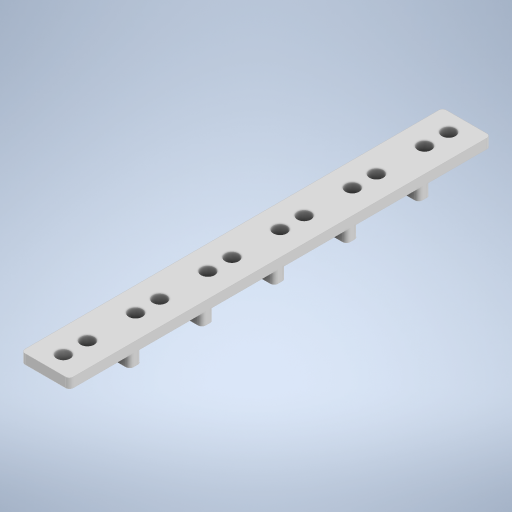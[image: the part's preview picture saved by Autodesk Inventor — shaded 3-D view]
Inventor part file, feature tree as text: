
AUTODESK INVENTOR PART (.ipt)
format: ipt  version: 2024.2 (Build 282272000, 272)  size: 366,592 bytes
history: native  units: mm
features: extrude x2, other x1, sketch x1, fillet x1
ambient origin geometry x8: Origin, YZ Plane, XZ Plane, XY Plane, X Axis, Y Axis, Z Axis, Center Point
bodies: Body1 (feature_tree)
feature tree (5):
  other  "Bryła1"
  sketch  "Szkic1"
  extrude  "Wyciągnięcie proste1"  Depth=20.0mm
  extrude  "Wyciągnięcie proste2"  Depth=25.0mm
  fillet  "Zaokrąglenie1"  Radius=5.0mm
